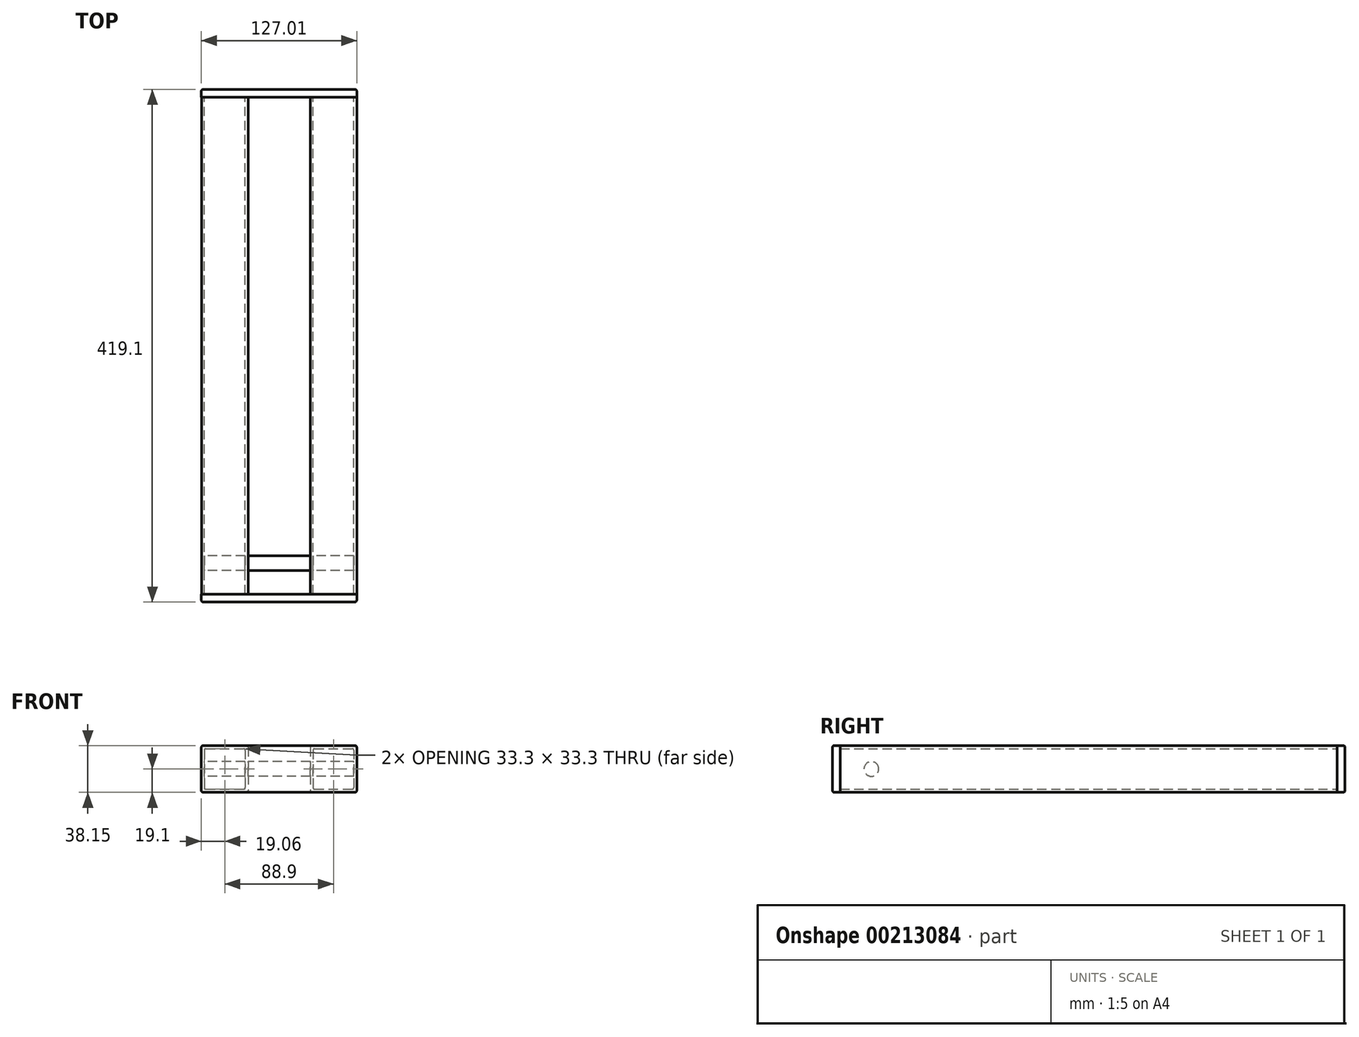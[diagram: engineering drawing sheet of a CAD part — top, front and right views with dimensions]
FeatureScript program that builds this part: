
annotation { "Feature Type Name" : "Feature", "Feature Type Description" : "" }
export const myFeature = defineFeature(function(context is Context, id is Id, definition is map)
    precondition{}
    {
        {
            var Q0;
            Q0=qCreatedBy(makeId("Front.planeOp"),FACE);
            var sketch = newSketch(context, id + "F0", { "sketchPlane" : qUnion([Q0])});
            skLineSegment(sketch, "E0.bottom", {"start": v(1.27, 0) * mm, "end": v(36.83, 0) * mm});
            skLineSegment(sketch, "E0.top", {"start": v(1.27, -38.1) * mm, "end": v(36.83, -38.1) * mm});
            skLineSegment(sketch, "E0.left", {"start": v(0, -1.27) * mm, "end": v(0, -36.83) * mm});
            skLineSegment(sketch, "E0.right", {"start": v(38.1, -1.27) * mm, "end": v(38.1, -36.83) * mm});
            skLineSegment(sketch, "E1.0", {"start": v(3.67, -2.4) * mm, "end": v(34.43, -2.4) * mm});
            skLineSegment(sketch, "E1.1", {"start": v(2.4, -3.67) * mm, "end": v(2.4, -34.43) * mm});
            skLineSegment(sketch, "E1.2", {"start": v(3.67, -35.7) * mm, "end": v(34.43, -35.7) * mm});
            skLineSegment(sketch, "E1.3", {"start": v(35.7, -3.67) * mm, "end": v(35.7, -34.43) * mm});
            skPoint(sketch, "E2.visualSharp", {"position": v(0, 0) * mm});
            skArc(sketch, "E2.filletArc", {"start": v(1.27, 0) * mm, "mid": v(0.37, -0.37) * mm, "end": v(0, -1.27) * mm});
            skPoint(sketch, "E3.visualSharp", {"position": v(38.1, 0) * mm});
            skArc(sketch, "E3.filletArc", {"start": v(38.1, -1.27) * mm, "mid": v(37.73, -0.37) * mm, "end": v(36.83, 0) * mm});
            skPoint(sketch, "E4.visualSharp", {"position": v(38.1, -38.1) * mm});
            skArc(sketch, "E4.filletArc", {"start": v(36.83, -38.1) * mm, "mid": v(37.73, -37.73) * mm, "end": v(38.1, -36.83) * mm});
            skPoint(sketch, "E5.visualSharp", {"position": v(0, -38.1) * mm});
            skArc(sketch, "E5.filletArc", {"start": v(0, -36.83) * mm, "mid": v(0.37, -37.73) * mm, "end": v(1.27, -38.1) * mm});
            skPoint(sketch, "E6.visualSharp", {"position": v(2.4, -35.7) * mm});
            skArc(sketch, "E6.filletArc", {"start": v(2.4, -34.43) * mm, "mid": v(2.77, -35.33) * mm, "end": v(3.67, -35.7) * mm});
            skPoint(sketch, "E7.visualSharp", {"position": v(2.4, -2.4) * mm});
            skArc(sketch, "E7.filletArc", {"start": v(3.67, -2.4) * mm, "mid": v(2.77, -2.77) * mm, "end": v(2.4, -3.67) * mm});
            skPoint(sketch, "E8.visualSharp", {"position": v(35.7, -2.4) * mm});
            skArc(sketch, "E8.filletArc", {"start": v(35.7, -3.67) * mm, "mid": v(35.33, -2.77) * mm, "end": v(34.43, -2.4) * mm});
            skPoint(sketch, "E9.visualSharp", {"position": v(35.7, -35.7) * mm});
            skArc(sketch, "E9.filletArc", {"start": v(34.43, -35.7) * mm, "mid": v(35.33, -35.33) * mm, "end": v(35.7, -34.43) * mm});
            skSolve(sketch);
        }
        {
            var Q0;
            Q0=makeQuery(id+"F0.imprint","IMPRINT",FACE,{"disambiguationData":[TD([[makeQuery(id+"F0.imprint","IMPRINT",EDGE,{"derivedFrom":sQuery(id+"F0.wireOp",EDGE,"E0.bottom")}),-1.0]])]});
            extrude(context, id + "F1", {"entities" : qUnion([Q0]), "depth" : 406.4 * mm});
        }
        {
            var Q0;
            Q0=makeQuery(id+"F1.opExtrude","SWEPT_BODY",BODY,{"disambiguationData":[OSD([sQuery(id+"F0.wireOp",EDGE,"E0.bottom"),sQuery(id+"F0.wireOp",EDGE,"E0.top"),sQuery(id+"F0.wireOp",EDGE,"E0.left"),sQuery(id+"F0.wireOp",EDGE,"E0.right"),sQuery(id+"F0.wireOp",EDGE,"E1.0"),sQuery(id+"F0.wireOp",EDGE,"E1.1"),sQuery(id+"F0.wireOp",EDGE,"E1.2"),sQuery(id+"F0.wireOp",EDGE,"E1.3"),sQuery(id+"F0.wireOp",EDGE,"E2.filletArc"),sQuery(id+"F0.wireOp",EDGE,"E3.filletArc"),sQuery(id+"F0.wireOp",EDGE,"E4.filletArc"),sQuery(id+"F0.wireOp",EDGE,"E5.filletArc"),sQuery(id+"F0.wireOp",EDGE,"E6.filletArc"),sQuery(id+"F0.wireOp",EDGE,"E7.filletArc"),sQuery(id+"F0.wireOp",EDGE,"E8.filletArc"),sQuery(id+"F0.wireOp",EDGE,"E9.filletArc")])]});
            transform(context, id + "F2", {"entities" : qUnion([Q0]), "transformType" : TransformType.TRANSLATION_3D, "dx" : -88.9 * mm, "dy" : 0 * mm, "dz" : 0 * mm, "makeCopy" : true});
        }
        {
            var Q0;
            Q0=makeQuery(id+"F1.opExtrude","CAP_FACE",FACE,{"disambiguationData":[OSD([sQuery(id+"F0.wireOp",EDGE,"E0.bottom"),sQuery(id+"F0.wireOp",EDGE,"E0.top"),sQuery(id+"F0.wireOp",EDGE,"E0.left"),sQuery(id+"F0.wireOp",EDGE,"E0.right"),sQuery(id+"F0.wireOp",EDGE,"E1.0"),sQuery(id+"F0.wireOp",EDGE,"E1.1"),sQuery(id+"F0.wireOp",EDGE,"E1.2"),sQuery(id+"F0.wireOp",EDGE,"E1.3"),sQuery(id+"F0.wireOp",EDGE,"E2.filletArc"),sQuery(id+"F0.wireOp",EDGE,"E3.filletArc"),sQuery(id+"F0.wireOp",EDGE,"E4.filletArc"),sQuery(id+"F0.wireOp",EDGE,"E5.filletArc"),sQuery(id+"F0.wireOp",EDGE,"E6.filletArc"),sQuery(id+"F0.wireOp",EDGE,"E7.filletArc"),sQuery(id+"F0.wireOp",EDGE,"E8.filletArc"),sQuery(id+"F0.wireOp",EDGE,"E9.filletArc")])],"isStart":true});
            var sketch = newSketch(context, id + "F3", { "sketchPlane" : qUnion([Q0])});
            skLineSegment(sketch, "E10.bottom", {"start": v(-36.83, 0) * mm, "end": v(-38.1, 0) * mm});
            skLineSegment(sketch, "E10.top", {"start": v(-36.83, 0) * mm, "end": v(-38.1, 0) * mm});
            skLineSegment(sketch, "E10.left", {"start": v(-36.83, 0) * mm, "end": v(-36.83, 0) * mm});
            skLineSegment(sketch, "E10.right", {"start": v(-38.1, 0) * mm, "end": v(-38.1, 0) * mm});
            skLineSegment(sketch, "E11.bottom", {"start": v(-38.1, 0) * mm, "end": v(88.9, 0) * mm});
            skLineSegment(sketch, "E11.top", {"start": v(-38.1, -38.15) * mm, "end": v(88.9, -38.15) * mm});
            skLineSegment(sketch, "E11.left", {"start": v(-38.1, 0) * mm, "end": v(-38.1, -38.15) * mm});
            skLineSegment(sketch, "E11.right", {"start": v(88.9, 0) * mm, "end": v(88.9, -38.15) * mm});
            skSolve(sketch);
        }
        {
            var Q0;
            Q0 = qSketchRegion(id + "F3", true);
            extrude(context, id + "F4", {"entities" : qUnion([Q0]), "depth" : 6.35 * mm});
        }
        {
            var Q0;
            Q0=makeQuery(id+"F4.opExtrude","SWEPT_BODY",BODY,{"disambiguationData":[OSD([sQuery(id+"F3.wireOp",EDGE,"E11.bottom"),sQuery(id+"F3.wireOp",EDGE,"E11.top"),sQuery(id+"F3.wireOp",EDGE,"E11.left"),sQuery(id+"F3.wireOp",EDGE,"E11.right")])]});
            transform(context, id + "F5", {"entities" : qUnion([Q0]), "transformType" : TransformType.TRANSLATION_3D, "dx" : 0 * mm, "dy" : -412.75 * mm, "dz" : 0 * mm, "makeCopy" : true});
        }
        {
            var Q0;
            Q0=makeQuery(id+"F2.opPattern","COPY",FACE,{"derivedFrom":makeQuery(id+"F1.opExtrude","SWEPT_FACE",FACE,{"disambiguationData":[OSD([sQuery(id+"F0.wireOp",EDGE,"E0.left")])]}),"instanceName":"1"});
            var sketch = newSketch(context, id + "F6", { "sketchPlane" : qUnion([Q0])});
            skLineSegment(sketch, "E12", {"start": v(406.4, -19.05) * mm, "end": v(-26.17, -19.05) * mm, "construction": true});
            skPoint(sketch, "E12.endSnap0", {"position": v(0, -19.05) * mm});
            skLineSegment(sketch, "E13", {"start": v(381, 17.94) * mm, "end": v(381, -71.13) * mm, "construction": true});
            skPoint(sketch, "E14", {"position": v(381, -19.05) * mm});
            skCircle(sketch, "E15", {"center": v(381, -19.05) * mm, "radius": 6 * mm});
            skSolve(sketch);
        }
        {
            var Q0;
            Q0=makeQuery(id+"F6.imprint","IMPRINT",FACE,{"disambiguationData":[TD([[makeQuery(id+"F6.imprint","IMPRINT",EDGE,{"derivedFrom":sQuery(id+"F6.wireOp",EDGE,"E15")}),1.0]])]});
            var Q1;
            Q1=sQuery(id+"F6.wireOp",EDGE,"E15");
            extrude(context, id + "F7", {"entities" : qUnion([Q0]), "operationType" : NewBodyOperationType.ADD, "surfaceEntities" : qUnion([Q1]), "oppositeDirection" : true, "depth" : 127 * mm});
        }
        {
            var Q0;
            Q0=makeQuery(id+"F4.opExtrude","CAP_EDGE",EDGE,{"disambiguationData":[OSD([sQuery(id+"F3.wireOp",EDGE,"E11.bottom")])],"isStart":false});
            var Q1;
            Q1=makeQuery(id+"F4.opExtrude","CAP_EDGE",EDGE,{"disambiguationData":[OSD([sQuery(id+"F3.wireOp",EDGE,"E11.top")])],"isStart":false});
            var Q2;
            Q2=makeQuery(id+"F4.opExtrude","CAP_EDGE",EDGE,{"disambiguationData":[OSD([sQuery(id+"F3.wireOp",EDGE,"E11.right")])],"isStart":false});
            var Q3;
            Q3=makeQuery(id+"F4.opExtrude","CAP_EDGE",EDGE,{"disambiguationData":[OSD([sQuery(id+"F3.wireOp",EDGE,"E11.left")])],"isStart":false});
            var Q4;
            Q4=makeQuery(id+"F5.opPattern","COPY",EDGE,{"derivedFrom":makeQuery(id+"F4.opExtrude","CAP_EDGE",EDGE,{"disambiguationData":[OSD([sQuery(id+"F3.wireOp",EDGE,"E11.right")])],"isStart":true}),"instanceName":"1"});
            var Q5;
            Q5=makeQuery(id+"F5.opPattern","COPY",EDGE,{"derivedFrom":makeQuery(id+"F4.opExtrude","CAP_EDGE",EDGE,{"disambiguationData":[OSD([sQuery(id+"F3.wireOp",EDGE,"E11.bottom")])],"isStart":true}),"instanceName":"1"});
            var Q6;
            Q6=makeQuery(id+"F5.opPattern","COPY",EDGE,{"derivedFrom":makeQuery(id+"F4.opExtrude","CAP_EDGE",EDGE,{"disambiguationData":[OSD([sQuery(id+"F3.wireOp",EDGE,"E11.top")])],"isStart":true}),"instanceName":"1"});
            var Q7;
            Q7=makeQuery(id+"F5.opPattern","COPY",EDGE,{"derivedFrom":makeQuery(id+"F4.opExtrude","CAP_EDGE",EDGE,{"disambiguationData":[OSD([sQuery(id+"F3.wireOp",EDGE,"E11.left")])],"isStart":true}),"instanceName":"1"});
            var Q8;
            Q8=makeQuery(id+"F5.opPattern","COPY",EDGE,{"derivedFrom":makeQuery(id+"F4.opExtrude","SWEPT_EDGE",EDGE,{"disambiguationData":[OSD([sQuery(id+"F3.wireOp",EDGE,"E11.bottom"),sQuery(id+"F3.wireOp",EDGE,"E11.right")])]}),"instanceName":"1"});
            var Q9;
            Q9=makeQuery(id+"F5.opPattern","COPY",EDGE,{"derivedFrom":makeQuery(id+"F4.opExtrude","SWEPT_EDGE",EDGE,{"disambiguationData":[OSD([sQuery(id+"F3.wireOp",EDGE,"E11.top"),sQuery(id+"F3.wireOp",EDGE,"E11.right")])]}),"instanceName":"1"});
            var Q10;
            Q10=makeQuery(id+"F5.opPattern","COPY",EDGE,{"derivedFrom":makeQuery(id+"F4.opExtrude","SWEPT_EDGE",EDGE,{"disambiguationData":[OSD([sQuery(id+"F3.wireOp",EDGE,"E11.bottom"),sQuery(id+"F3.wireOp",EDGE,"E11.left")])]}),"instanceName":"1"});
            var Q11;
            Q11=makeQuery(id+"F5.opPattern","COPY",EDGE,{"derivedFrom":makeQuery(id+"F4.opExtrude","SWEPT_EDGE",EDGE,{"disambiguationData":[OSD([sQuery(id+"F3.wireOp",EDGE,"E11.top"),sQuery(id+"F3.wireOp",EDGE,"E11.left")])]}),"instanceName":"1"});
            var Q12;
            Q12=makeQuery(id+"F4.opExtrude","SWEPT_EDGE",EDGE,{"disambiguationData":[OSD([sQuery(id+"F3.wireOp",EDGE,"E11.bottom"),sQuery(id+"F3.wireOp",EDGE,"E11.right")])]});
            var Q13;
            Q13=makeQuery(id+"F4.opExtrude","SWEPT_EDGE",EDGE,{"disambiguationData":[OSD([sQuery(id+"F3.wireOp",EDGE,"E11.bottom"),sQuery(id+"F3.wireOp",EDGE,"E11.left")])]});
            var Q14;
            Q14=makeQuery(id+"F4.opExtrude","SWEPT_EDGE",EDGE,{"disambiguationData":[OSD([sQuery(id+"F3.wireOp",EDGE,"E11.top"),sQuery(id+"F3.wireOp",EDGE,"E11.right")])]});
            var Q15;
            Q15=makeQuery(id+"F4.opExtrude","SWEPT_EDGE",EDGE,{"disambiguationData":[OSD([sQuery(id+"F3.wireOp",EDGE,"E11.top"),sQuery(id+"F3.wireOp",EDGE,"E11.left")])]});
            fillet(context, id + "F8", {"entities" : qUnion([Q0, Q1, Q2, Q3, Q4, Q5, Q6, Q7, Q8, Q9, Q10, Q11, Q12, Q13, Q14, Q15]), "radius" : 1.27 * mm, "tangentPropagation" : true, "allowEdgeOverflow" : false});
        }
    });
